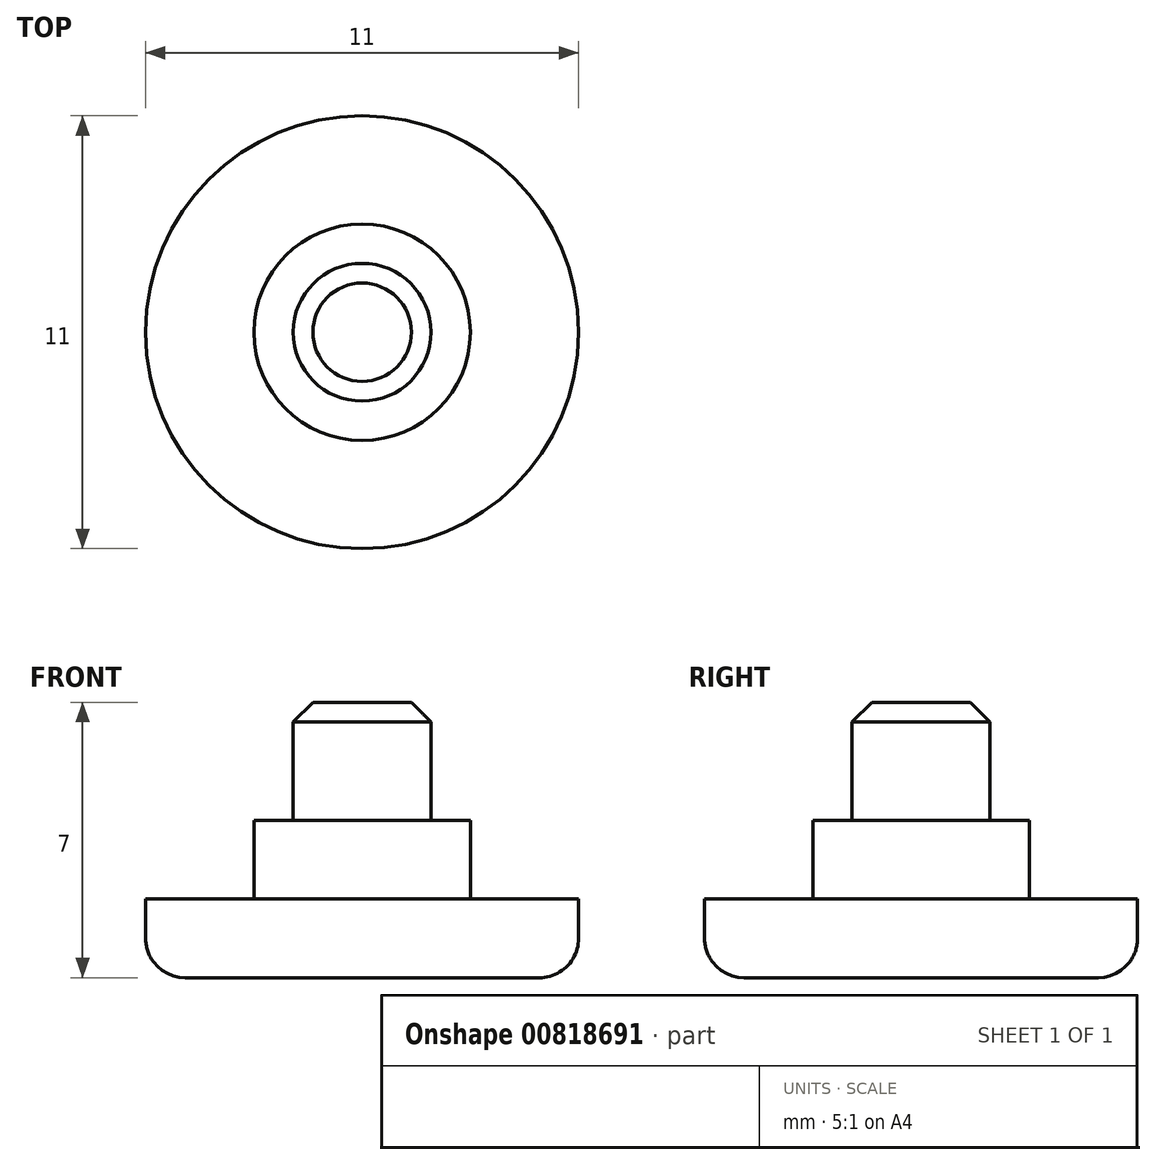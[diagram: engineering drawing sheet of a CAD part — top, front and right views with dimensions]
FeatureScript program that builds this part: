
annotation { "Feature Type Name" : "Feature", "Feature Type Description" : "" }
export const myFeature = defineFeature(function(context is Context, id is Id, definition is map)
    precondition{}
    {
        {
            var Q0;
            Q0=qCreatedBy(makeId("Top.planeOp"),FACE);
            var sketch = newSketch(context, id + "F0", { "sketchPlane" : qUnion([Q0])});
            skCircle(sketch, "E0", {"center": v(0, 0) * mm, "radius": 5.5 * mm});
            skSolve(sketch);
        }
        {
            var Q0;
            Q0=makeQuery(id+"F0.imprint","IMPRINT",FACE,{"disambiguationData":[TD([[makeQuery(id+"F0.imprint","IMPRINT",EDGE,{"derivedFrom":sQuery(id+"F0.wireOp",EDGE,"E0")}),1.0]])]});
            extrude(context, id + "F1", {"entities" : qUnion([Q0]), "depth" : 2 * mm, "offsetDistance" : 25 * mm});
        }
        {
            var Q0;
            Q0=makeQuery(id+"F1.opExtrude","CAP_FACE",FACE,{"disambiguationData":[OSD([sQuery(id+"F0.wireOp",EDGE,"E0")])],"isStart":false});
            var sketch = newSketch(context, id + "F2", { "sketchPlane" : qUnion([Q0])});
            skCircle(sketch, "E1", {"center": v(0, 0) * mm, "radius": 2.75 * mm});
            skSolve(sketch);
        }
        {
            var Q0;
            Q0=makeQuery(id+"F2.imprint","IMPRINT",FACE,{"disambiguationData":[TD([[makeQuery(id+"F2.imprint","IMPRINT",EDGE,{"derivedFrom":sQuery(id+"F2.wireOp",EDGE,"E1")}),1.0]])]});
            extrude(context, id + "F3", {"entities" : qUnion([Q0]), "operationType" : NewBodyOperationType.ADD, "depth" : 2 * mm, "offsetDistance" : 25 * mm});
        }
        {
            var Q0;
            Q0=makeQuery(id+"F3.opExtrude","CAP_FACE",FACE,{"disambiguationData":[OSD([sQuery(id+"F2.wireOp",EDGE,"E1")])],"isStart":false});
            var sketch = newSketch(context, id + "F4", { "sketchPlane" : qUnion([Q0])});
            skCircle(sketch, "E2", {"center": v(0, 0) * mm, "radius": 1.75 * mm});
            skSolve(sketch);
        }
        {
            var Q0;
            Q0=makeQuery(id+"F4.imprint","IMPRINT",FACE,{"disambiguationData":[TD([[makeQuery(id+"F4.imprint","IMPRINT",EDGE,{"derivedFrom":sQuery(id+"F4.wireOp",EDGE,"E2")}),1.0]])]});
            extrude(context, id + "F5", {"entities" : qUnion([Q0]), "operationType" : NewBodyOperationType.ADD, "depth" : 3 * mm, "offsetDistance" : 25 * mm});
        }
        {
            var Q0;
            Q0=makeQuery(id+"F1.opExtrude","CAP_EDGE",EDGE,{"disambiguationData":[OSD([sQuery(id+"F0.wireOp",EDGE,"E0")])],"isStart":true});
            fillet(context, id + "F6", {"entities" : qUnion([Q0]), "radius" : 1 * mm, "tangentPropagation" : true, "allowEdgeOverflow" : false});
        }
        {
            var Q0;
            Q0=makeQuery(id+"F5.opExtrude","CAP_EDGE",EDGE,{"disambiguationData":[OSD([sQuery(id+"F4.wireOp",EDGE,"E2")])],"isStart":false});
            chamfer(context, id + "F7", {"entities" : qUnion([Q0]), "width" : .5 * mm, "tangentPropagation" : true});
        }
    });
